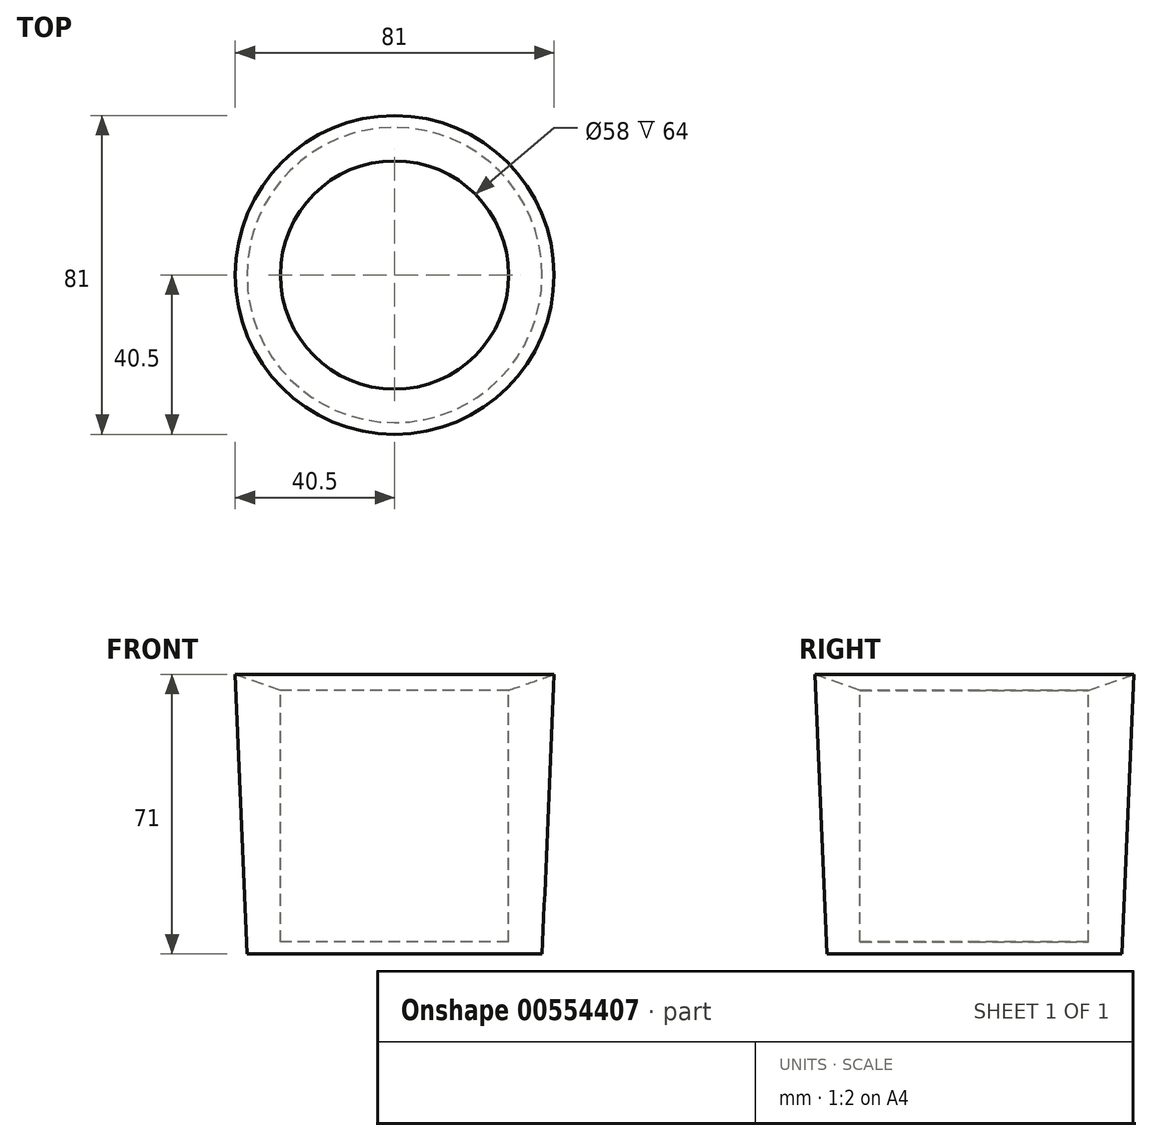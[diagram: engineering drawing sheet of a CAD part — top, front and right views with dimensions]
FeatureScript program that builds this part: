
annotation { "Feature Type Name" : "Feature", "Feature Type Description" : "" }
export const myFeature = defineFeature(function(context is Context, id is Id, definition is map)
    precondition{}
    {
        {
            var Q0;
            Q0=qCreatedBy(makeId("Right.planeOp"),FACE);
            var sketch = newSketch(context, id + "F0", { "sketchPlane" : qUnion([Q0])});
            skLineSegment(sketch, "E0", {"start": v(-40.5, 71) * mm, "end": v(-29, 67) * mm});
            skLineSegment(sketch, "E1", {"start": v(-29, 67) * mm, "end": v(-29, 3) * mm});
            skLineSegment(sketch, "E2", {"start": v(-29, 3) * mm, "end": v(0, 3) * mm});
            skLineSegment(sketch, "E3", {"start": v(0, 3) * mm, "end": v(0, 0) * mm});
            skLineSegment(sketch, "E4", {"start": v(0, 0) * mm, "end": v(-37.5, 0) * mm});
            skLineSegment(sketch, "E5", {"start": v(-40.5, 71) * mm, "end": v(-37.5, 0) * mm});
            skSolve(sketch);
        }
        {
            var Q0;
            Q0 = qSketchRegion(id + "F0", true);
            var Q1;
            Q1=makeQuery(id+"F0.imprint","IMPRINT",FACE,{"disambiguationData":[TD([[makeQuery(id+"F0.imprint","IMPRINT",EDGE,{"derivedFrom":sQuery(id+"F0.wireOp",EDGE,"E0")}),-1.0]])]});
            var Q2;
            Q2=sQuery(id+"F0.wireOp",EDGE,"E3");
            revolve(context, id + "F1", {"entities" : qUnion([Q0, Q1]), "axis" : qUnion([Q2]), "revolveType" : RevolveType.FULL});
        }
    });
